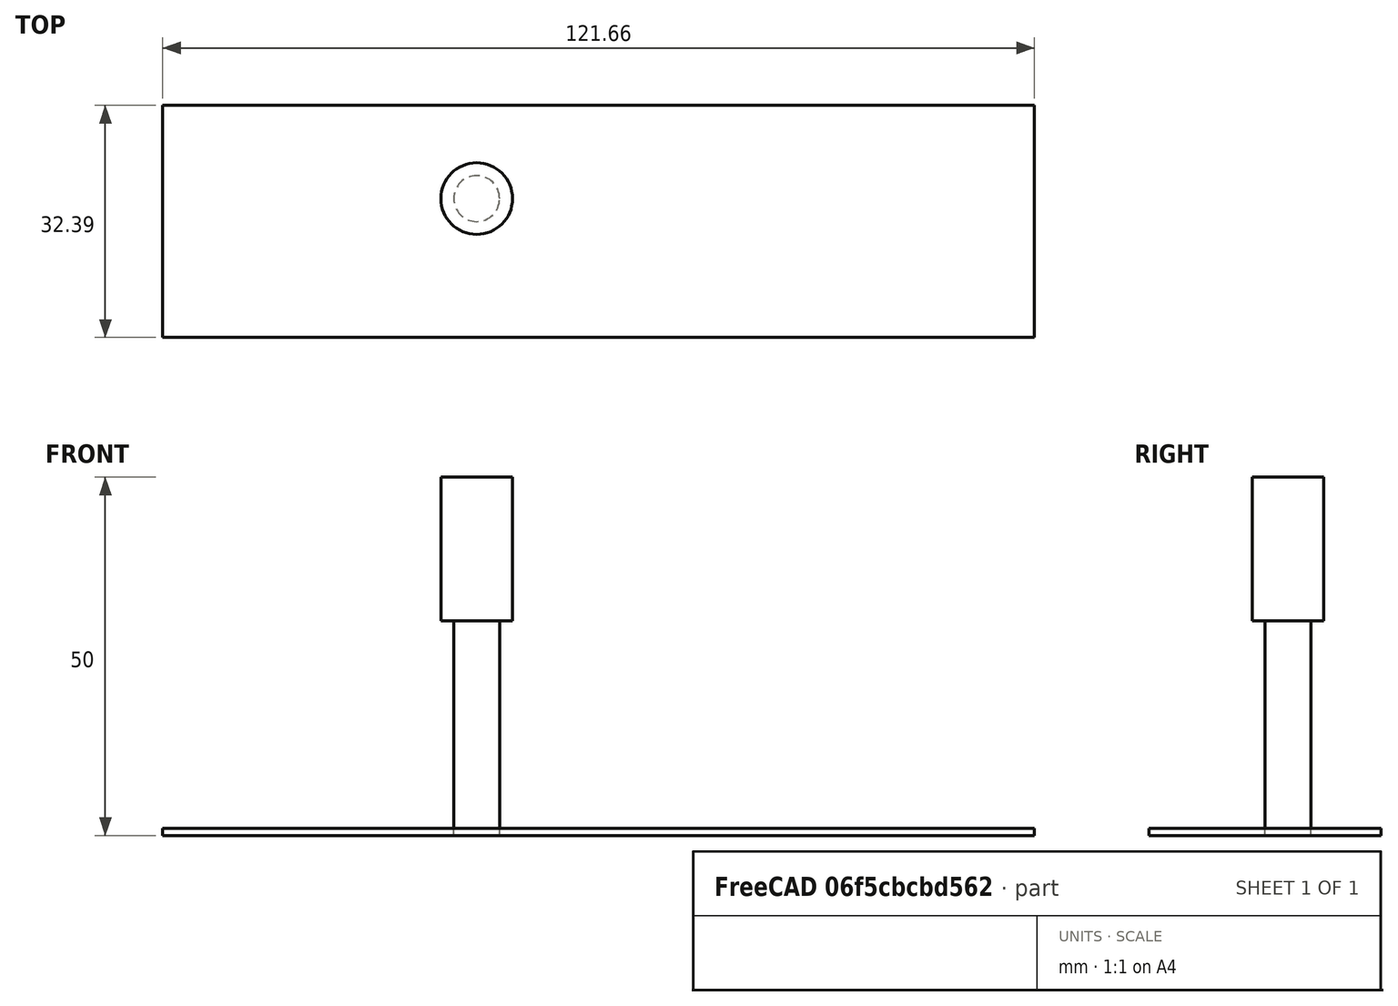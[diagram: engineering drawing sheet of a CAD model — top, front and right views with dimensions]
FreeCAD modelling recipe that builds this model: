
FCSTD DOCUMENT  (FreeCAD 0.20RUnknown)
Label: snake1
License: All rights reserved
LicenseURL: http://en.wikipedia.org/wiki/All_rights_reserved
objects: Part::FeaturePython×3, App::DocumentObjectGroup×3, Path::FeaturePython×3, Sketcher::SketchObject×1, PartDesign::Body×1, Part::Offset2D×1, App::FeaturePython×1, Mesh::FeaturePython×1
note: 7 computed .brp shape members not serialized (recipe doc carries the construction recipe); baked Part::Feature solids carry a one-line shape summary decoded from their .brp

FEATURE [Sketcher::SketchObject] Sketch
  FullyConstrained = false
  MapMode = 5
  Support = -> [XY_Plane]
  sketch-geometry (17):
    g0-g8: Circle x9 (B-spline internal-alignment scaffolding for g9; pole/knot coordinates omitted)
    g9: BSplineCurve PolesCount=9 KnotsCount=7 Degree=3 IsPeriodic=0
    g10-g16: GeomPoint x7 (B-spline internal-alignment scaffolding for g9; pole/knot coordinates omitted)
  constraints (4):
    c: Weight(g0) = 1
    c: Equal(g0, g1-g8) x8
    c: InternalAlignment(g0-g8 -> g9) x9
    c: InternalAlignment(g10-g16 -> g9) x7
FEATURE [PartDesign::Body] Body
  Group = -> [Sketch]
  Origin = -> Origin
FEATURE [Part::Offset2D] Offset2D
  Fill = false
  Intersection = false
  Join = 0
  Mode = 1
  SelfIntersection = false
  Source = -> Sketch
  Value = 3.3
  expr: Value = 3.3
FEATURE [App::FeaturePython] SetupSheet  # Path/CAM operation (typed FeaturePython)
  ClearanceHeightExpression = OpStockZMax+SetupSheet.ClearanceHeightOffset
  ClearanceHeightOffset = 5
  CoolantMode = 0
  CoolantModes = None | Flood | Mist
  FinalDepthExpression = OpFinalDepth
  HorizRapid = 0
  SafeHeightExpression = OpStockZMax+SetupSheet.SafeHeightOffset
  SafeHeightOffset = 3
  StartDepthExpression = OpStartDepth
  StepDownExpression = OpToolDiameter
  VertRapid = 0
FEATURE [Part::FeaturePython] Clone  label="Model-Offset2D"  # Draft clone (typed FeaturePython)
  AttacherType = Attacher::AttachEngine3D
  Fuse = false
  Objects = -> [Offset2D]
  PathResource = Model
  Scale = (1,1,1)
FEATURE [App::DocumentObjectGroup] Model
  Group = -> [Clone]
FEATURE [Part::FeaturePython] Stock001  # WARN: FeaturePython — macro-defined, semantics opaque (R4)
  Height = 1
  Length = 121.66
  Placement = pos=(-43.8248,-19.3779,0) rot=(0,0,1;0rad)
  StockType = CreateBox
  Width = 32.39
FEATURE [Part::FeaturePython] ToolBit001  label="6.4mm Endmill"  # Path/CAM toolbit (typed FeaturePython)
  BitPropertyNames = Chipload | CuttingEdgeHeight | Diameter | Flutes | Length | Material | ShankDiameter | SpindleDirection
  BitShape = <path>
  Chipload = 0
  CuttingEdgeHeight = 30
  Diameter = 6.4
  File = <userpath>/Documents/Sherline/FreeCAD/Bit/6.4mm_Endmill.fctb
  Flutes = 0
  Length = 50
  Material = 0
  ShankDiameter = 10
  ShapeName = endmill
  SpindleDirection = 0
FEATURE [Path::FeaturePython] __4mm_Endmill  label="6.4mm Endmill001"  # Path/CAM operation (typed FeaturePython)
  HorizFeed = 15
  HorizRapid = 0
  SpindleDir = 0
  SpindleSpeed = 12000
  Tool = -> ToolBit001
  ToolNumber = 2
  VertFeed = 5
  VertRapid = 0
  expr: HorizRapid = SetupSheet.HorizRapid
  expr: VertRapid = SetupSheet.VertRapid
FEATURE [App::DocumentObjectGroup] Tools
  Group = -> [__4mm_Endmill]
FEATURE [Path::FeaturePython] Profile  # Path/CAM operation (typed FeaturePython)
  Active = true
  AreaParams:
    Tolerance = 1e-07
    FitArcs = True
    Simplify = False
    CleanDistance = 0.0
    Accuracy = 0.01
    Unit = 1.0
    MinArcPoints = 4
    MaxArcPoints = 100
    ClipperScale = 10000000.0
    Fill = 0
    Coplanar = 0
    Reorient = True
    Outline = False
    Explode = False
    OpenMode = 0
    Deflection = 0.01
    SubjectFill = 0
    ClipFill = 0
    Offset = -3.2
    ExtraPass = 0
    Stepover = 0.0
    LastStepover = 0.0
    JoinType = 0
    EndType = 0
    MiterLimit = 2.0
    RoundPrecision = 0.0
    PocketMode = 0
    ToolRadius = 1.0
    PocketExtraOffset = 0.0
    PocketStepover = 0.0
    PocketLastStepover = 0.0
    FromCenter = False
    Angle = 45.0
    AngleShift = 0.0
    Shift = 0.0
    Thicken = False
    SectionCount = -1
    Stepdown = 1.0
    SectionOffset = 0.0
    SectionTolerance = 1e-06
    SectionMode = 2
    Project = False
  Base = -> [Clone]
  ClearanceHeight = 6
  CoolantMode = 0
  CycleTime = 00:00:42
  Direction = 0
  FinalDepth = 0
  HandleMultipleFeatures = 0
  JoinType = 0
  MiterLimit = 0.1
  OffsetExtra = 0
  OpFinalDepth = 0
  OpStartDepth = 1
  OpStockZMax = 1
  OpStockZMin = 0
  OpToolDiameter = 6.4
  PathParams = {'orientation': 1, 'feedrate': 15.0, 'feedrate_v': 5.0, 'verbose': True, 'resume_height': 4.0, 'retraction': 6.0, 'return_end': True, 'preamble': False}
  SafeHeight = 4
  Side = 1
  SplitArcs = false
  StartDepth = 6
  StartPoint = (0,0,0)
  StepDown = 3
  ToolController = -> __4mm_Endmill
  UseComp = true
  UseStartPoint = false
  processCircles = false
  processHoles = false
  processPerimeter = true
  expr: ClearanceHeight = OpStockZMax + SetupSheet.ClearanceHeightOffset
  expr: FinalDepth = OpFinalDepth
  expr: SafeHeight = OpStockZMax + SetupSheet.SafeHeightOffset
  expr: StartDepth = 6
  expr: StepDown = 3
FEATURE [App::DocumentObjectGroup] Operations
  Group = -> [Profile]
FEATURE [Path::FeaturePython] Job  # Path/CAM operation (typed FeaturePython)
  CycleTime = 00:00:42
  Fixtures = G54
  GeometryTolerance = 0.01
  JobType = 0
  Model = -> Model
  Operations = -> Operations
  OrderOutputBy = 0
  PostProcessor = 2
  PostProcessorOutputFile = %D/%d.ngc
  SetupSheet = -> SetupSheet
  SplitOutput = false
  Stock = -> Stock001
  Tools = -> Tools
FEATURE [Mesh::FeaturePython] CutMaterial  # WARN: FeaturePython — macro-defined, semantics opaque (R4)
note: 1 file-system path scrubbed to <path> (originals preserved in the JSON sidecar)
